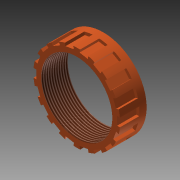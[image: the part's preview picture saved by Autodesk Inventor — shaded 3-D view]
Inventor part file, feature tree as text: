
AUTODESK INVENTOR PART (.ipt)
format: ipt  version: 2013 (Build 170138000, 138)  size: 206,336 bytes
history: native  units: mm
features: extrude x2, sketch x2, thread x1
ambient origin geometry x8: Origin, YZ Plane, XZ Plane, XY Plane, X Axis, Y Axis, Z Axis, Center Point
bodies: Solid1 (feature_tree)
feature tree (5):
  extrude  "Extrusion1"  Depth=36.0mm
  thread  "Thread1"  [1 undecoded]
  extrude  "Extrusion2"  Depth=3.5mm
  sketch  "Sketch1"  dims[d0=29.5mm d1=36.0mm d2=11.0mm d3=0.0mm]
  sketch  "Sketch2"  dims[d4=10.0mm d5=0.0mm d6=3.5mm d8=180.0mm d10=360.0deg d12=8.0mm d13=0.0mm]
note: 1 required parameter value undecoded (feature->parameter linkage not recoverable at this tier; creation-order binding heuristic only, values carry confidence <= 0.55)
